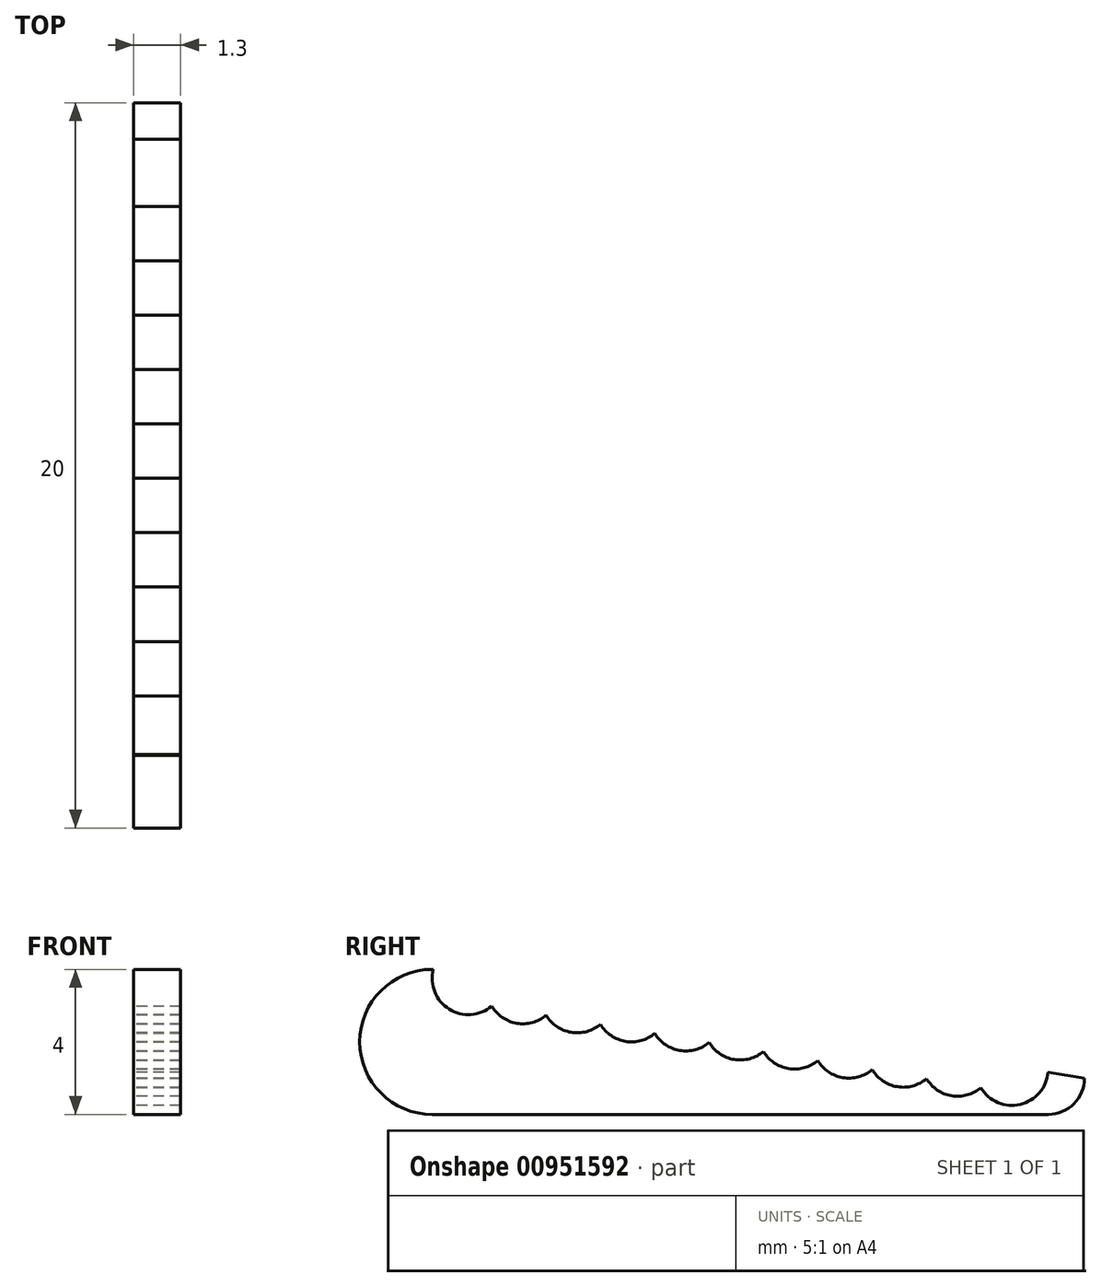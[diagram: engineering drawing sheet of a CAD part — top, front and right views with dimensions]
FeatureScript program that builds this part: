
annotation { "Feature Type Name" : "Feature", "Feature Type Description" : "" }
export const myFeature = defineFeature(function(context is Context, id is Id, definition is map)
    precondition{}
    {
        {
            var Q0;
            Q0=qCreatedBy(makeId("Right.planeOp"),FACE);
            var sketch = newSketch(context, id + "F0", { "sketchPlane" : qUnion([Q0])});
            skLineSegment(sketch, "E0.bottom", {"start": v(2, 0) * mm, "end": v(19, 0) * mm});
            skArc(sketch, "E1", {"start": v(2, 4) * mm, "mid": v(0, 2) * mm, "end": v(2, 0) * mm});
            skArc(sketch, "E2", {"start": v(19, 0) * mm, "mid": v(19.7, 0.3) * mm, "end": v(20, 1) * mm});
            skLineSegment(sketch, "E3", {"start": v(20, 1) * mm, "end": v(2, 4) * mm});
            skSolve(sketch);
        }
        {
            var Q0;
            Q0=qCreatedBy(makeId("Right.planeOp"),FACE);
            var sketch = newSketch(context, id + "F1", { "sketchPlane" : qUnion([Q0])});
            skCircle(sketch, "E4", {"center": v(9, 2.75) * mm, "radius": 1 * mm});
            skCircle(sketch, "E5", {"center": v(10.5, 2.5) * mm, "radius": 1 * mm});
            skCircle(sketch, "E6", {"center": v(12, 2.25) * mm, "radius": 1 * mm});
            skCircle(sketch, "E7", {"center": v(13.5, 2) * mm, "radius": 1 * mm});
            skCircle(sketch, "E8", {"center": v(15, 1.75) * mm, "radius": 1 * mm});
            skCircle(sketch, "E9", {"center": v(16.5, 1.5) * mm, "radius": 1 * mm});
            skCircle(sketch, "E10", {"center": v(18, 1.25) * mm, "radius": 1 * mm});
            skCircle(sketch, "E11", {"center": v(4.5, 3.5) * mm, "radius": 1 * mm});
            skCircle(sketch, "E12", {"center": v(3, 3.75) * mm, "radius": 1 * mm});
            skCircle(sketch, "E13", {"center": v(6, 3.25) * mm, "radius": 1 * mm});
            skCircle(sketch, "E14", {"center": v(7.5, 3) * mm, "radius": 1 * mm});
            skSolve(sketch);
        }
        {
            var Q0;
            Q0 = qSketchRegion(id + "F0", true);
            extrude(context, id + "F2", {"entities" : qUnion([Q0]), "depth" : 1.3 * mm, "offsetDistance" : 25 * mm});
        }
        {
            var Q0;
            Q0 = qSketchRegion(id + "F1", true);
            extrude(context, id + "F3", {"entities" : qUnion([Q0]), "operationType" : NewBodyOperationType.REMOVE, "endBound" : BoundingType.THROUGH_ALL, "depth" : 25 * mm, "offsetDistance" : 25 * mm});
        }
    });
